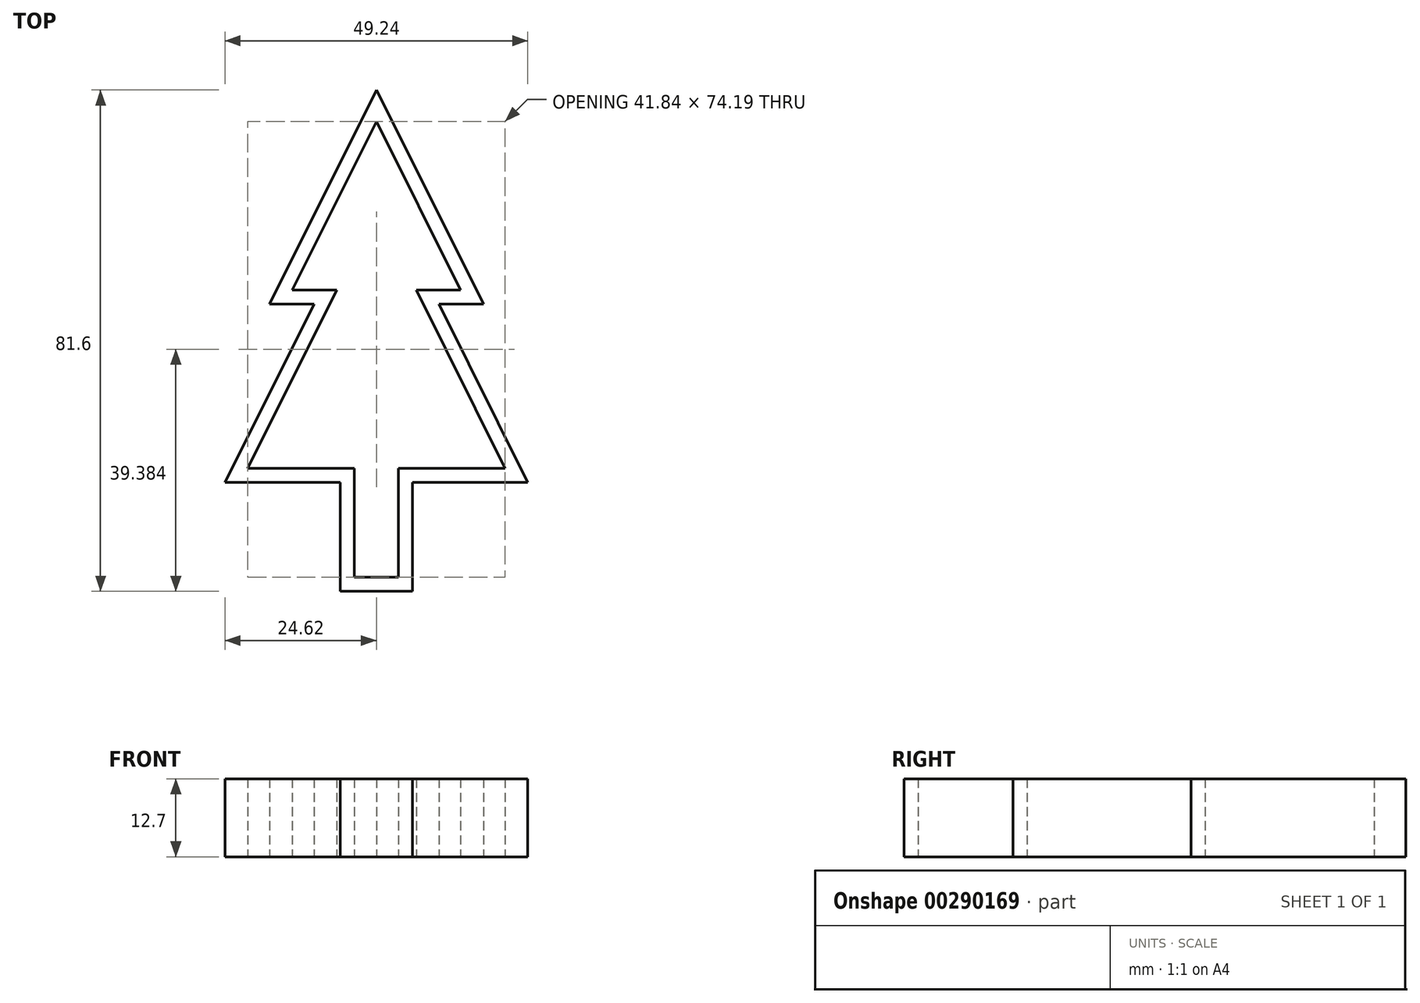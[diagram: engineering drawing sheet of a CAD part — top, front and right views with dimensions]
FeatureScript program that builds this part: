
annotation { "Feature Type Name" : "Feature", "Feature Type Description" : "" }
export const myFeature = defineFeature(function(context is Context, id is Id, definition is map)
    precondition{}
    {
        {
            var Q0;
            Q0=qCreatedBy(makeId("Top.planeOp"),FACE);
            var sketch = newSketch(context, id + "F0", { "sketchPlane" : qUnion([Q0])});
            skLineSegment(sketch, "E0", {"start": v(10.16, 0) * mm, "end": v(-10.16, 0) * mm});
            skLineSegment(sketch, "E1", {"start": v(-10.16, 0) * mm, "end": v(-24.62, 0) * mm});
            skLineSegment(sketch, "E2", {"start": v(-24.62, 0) * mm, "end": v(-10.16, 29) * mm});
            skLineSegment(sketch, "E3", {"start": v(-10.16, 29) * mm, "end": v(-17.39, 29) * mm});
            skPoint(sketch, "E3.endSnap0", {"position": v(-17.39, 14.5) * mm});
            skLineSegment(sketch, "E4", {"start": v(-17.39, 29) * mm, "end": v(0, 63.87) * mm});
            skLineSegment(sketch, "E5", {"start": v(0, 63.87) * mm, "end": v(0, 0) * mm, "construction": true});
            skLineSegment(sketch, "E6.MirrorCS", {"start": v(17.39, 29) * mm, "end": v(0, 63.87) * mm});
            skLineSegment(sketch, "E7.MirrorCS", {"start": v(10.16, 29) * mm, "end": v(17.39, 29) * mm});
            skLineSegment(sketch, "E8.MirrorCS", {"start": v(24.62, 0) * mm, "end": v(10.16, 29) * mm});
            skLineSegment(sketch, "E9.MirrorCS", {"start": v(10.16, 0) * mm, "end": v(24.62, 0) * mm});
            skPoint(sketch, "E10.start.orphan", {"position": v(0, -32.42) * mm});
            skLineSegment(sketch, "E11", {"start": v(-5.88, 0) * mm, "end": v(-5.88, -17.73) * mm});
            skLineSegment(sketch, "E12", {"start": v(-5.88, -17.73) * mm, "end": v(0, -17.73) * mm});
            skLineSegment(sketch, "E13.MirrorCS", {"start": v(5.88, -17.73) * mm, "end": v(0, -17.73) * mm});
            skLineSegment(sketch, "E14.MirrorCS", {"start": v(5.88, 0) * mm, "end": v(5.88, -17.73) * mm});
            skSolve(sketch);
        }
        {
            var Q0;
            {var subQ4=sQuery(id+"F0.wireOp",EDGE,"E1");Q0=makeQuery(id+"F0.imprint","IMPRINT",FACE,{"disambiguationData":[TD([[makeQuery(id+"F0.imprint","IMPRINT",EDGE,{"derivedFrom":subQ4}),-1.0]])]});}
            var Q1;
            {var subQ0=sQuery(id+"F0.wireOp",EDGE,"E11");Q1=makeQuery(id+"F0.imprint","IMPRINT",FACE,{"disambiguationData":[TD([[makeQuery(id+"F0.imprint","IMPRINT",EDGE,{"derivedFrom":subQ0}),1.0]])]});}
            extrude(context, id + "F1", {"entities" : qUnion([Q0, Q1]), "depth" : 12.7 * mm});
        }
        {
            var Q0;
            Q0=makeQuery(id+"F1.opExtrude","CAP_FACE",FACE,{"disambiguationData":[OSD([sQuery(id+"F0.wireOp",EDGE,"E0"),sQuery(id+"F0.wireOp",EDGE,"E1"),sQuery(id+"F0.wireOp",EDGE,"E2"),sQuery(id+"F0.wireOp",EDGE,"E3"),sQuery(id+"F0.wireOp",EDGE,"E4"),sQuery(id+"F0.wireOp",EDGE,"E6.MirrorCS"),sQuery(id+"F0.wireOp",EDGE,"E7.MirrorCS"),sQuery(id+"F0.wireOp",EDGE,"E8.MirrorCS"),sQuery(id+"F0.wireOp",EDGE,"E9.MirrorCS"),sQuery(id+"F0.wireOp",EDGE,"E11"),sQuery(id+"F0.wireOp",EDGE,"E12"),sQuery(id+"F0.wireOp",EDGE,"E13.MirrorCS"),sQuery(id+"F0.wireOp",EDGE,"E14.MirrorCS")])],"isStart":false});
            var Q1;
            Q1=makeQuery(id+"F1.opExtrude","CAP_FACE",FACE,{"disambiguationData":[OSD([sQuery(id+"F0.wireOp",EDGE,"E0"),sQuery(id+"F0.wireOp",EDGE,"E1"),sQuery(id+"F0.wireOp",EDGE,"E2"),sQuery(id+"F0.wireOp",EDGE,"E3"),sQuery(id+"F0.wireOp",EDGE,"E4"),sQuery(id+"F0.wireOp",EDGE,"E6.MirrorCS"),sQuery(id+"F0.wireOp",EDGE,"E7.MirrorCS"),sQuery(id+"F0.wireOp",EDGE,"E8.MirrorCS"),sQuery(id+"F0.wireOp",EDGE,"E9.MirrorCS"),sQuery(id+"F0.wireOp",EDGE,"E11"),sQuery(id+"F0.wireOp",EDGE,"E12"),sQuery(id+"F0.wireOp",EDGE,"E13.MirrorCS"),sQuery(id+"F0.wireOp",EDGE,"E14.MirrorCS")])],"isStart":true});
            shell(context, id + "F2", {"entities" : qUnion([Q0, Q1]), "thickness" : 2.3 * mm});
        }
    });
